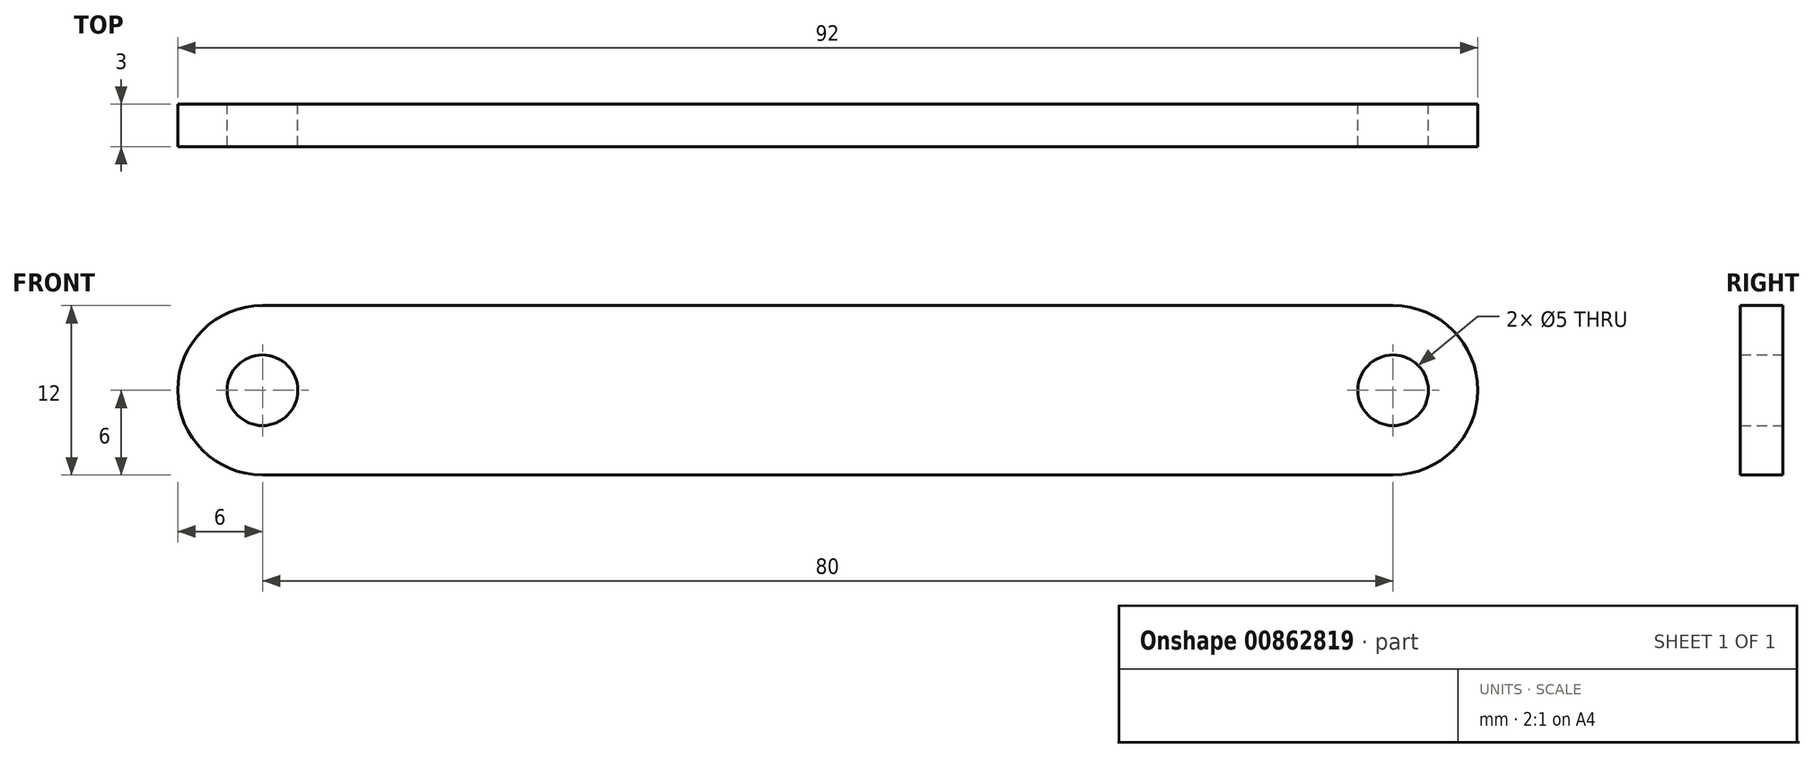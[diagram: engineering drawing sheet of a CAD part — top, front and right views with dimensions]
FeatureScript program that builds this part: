
annotation { "Feature Type Name" : "Feature", "Feature Type Description" : "" }
export const myFeature = defineFeature(function(context is Context, id is Id, definition is map)
    precondition{}
    {
        {
            var Q0;
            Q0=qCreatedBy(makeId("Front.planeOp"),FACE);
            var sketch = newSketch(context, id + "F0", { "sketchPlane" : qUnion([Q0])});
            skArc(sketch, "E0", {"start": v(0, 6) * mm, "mid": v(-6, 0) * mm, "end": v(0, -6) * mm});
            skArc(sketch, "E1", {"start": v(80, -6) * mm, "mid": v(86, 0) * mm, "end": v(80, 6) * mm});
            skLineSegment(sketch, "E2", {"start": v(0, 6) * mm, "end": v(80, 6) * mm});
            skLineSegment(sketch, "E3", {"start": v(0, -6) * mm, "end": v(80, -6) * mm});
            skCircle(sketch, "E4", {"center": v(0, 0) * mm, "radius": 2.5 * mm});
            skCircle(sketch, "E5", {"center": v(80, 0) * mm, "radius": 2.5 * mm});
            skSolve(sketch);
        }
        {
            var Q0;
            Q0 = qSketchRegion(id + "F0", true);
            extrude(context, id + "F1", {"entities" : qUnion([Q0]), "depth" : 3 * mm, "offsetDistance" : 25 * mm});
        }
    });
